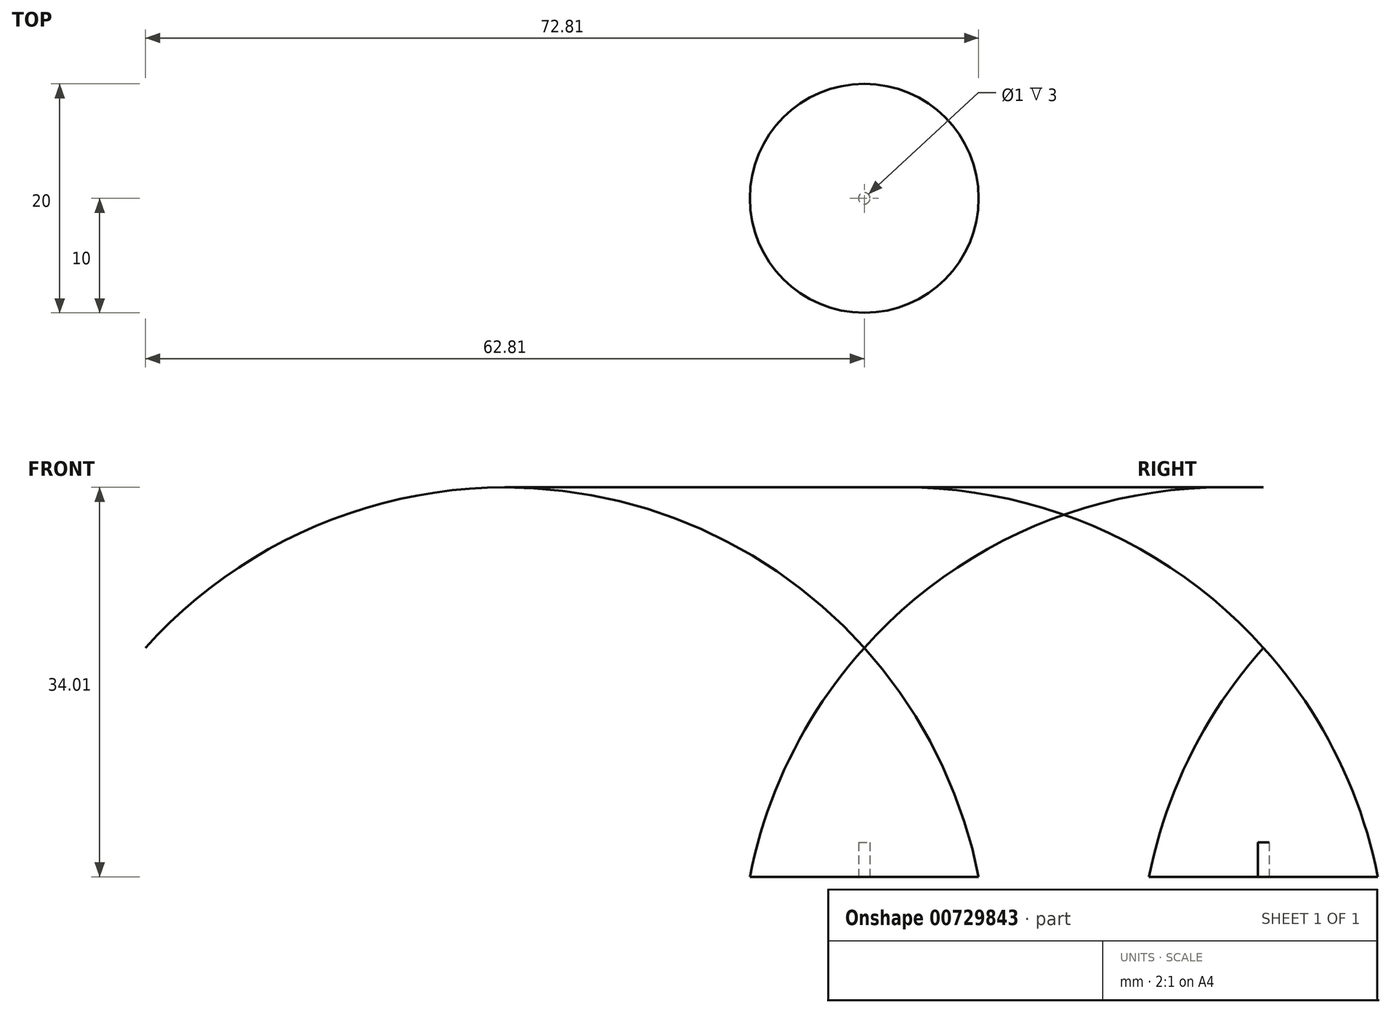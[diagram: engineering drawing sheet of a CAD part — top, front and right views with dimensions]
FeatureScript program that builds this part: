
annotation { "Feature Type Name" : "Feature", "Feature Type Description" : "" }
export const myFeature = defineFeature(function(context is Context, id is Id, definition is map)
    precondition{}
    {
        {
            var Q0;
            Q0=qCreatedBy(makeId("Front.planeOp"),FACE);
            var sketch = newSketch(context, id + "F0", { "sketchPlane" : qUnion([Q0])});
            skLineSegment(sketch, "E0", {"start": v(-0.5, 0) * mm, "end": v(-10, 0) * mm});
            skArc(sketch, "E1", {"start": v(0, 20) * mm, "mid": v(-6.35, 10.67) * mm, "end": v(-10, 0) * mm});
            skLineSegment(sketch, "E2", {"start": v(-0.5, 0) * mm, "end": v(-0.5, 3) * mm});
            skLineSegment(sketch, "E3", {"start": v(-0.5, 3) * mm, "end": v(0, 3) * mm});
            skLineSegment(sketch, "E4", {"start": v(0, 3) * mm, "end": v(0, 20) * mm});
            skSolve(sketch);
        }
        {
            var Q0;
            Q0=makeQuery(id+"F0.imprint","IMPRINT",FACE,{"disambiguationData":[TD([[makeQuery(id+"F0.imprint","IMPRINT",EDGE,{"derivedFrom":sQuery(id+"F0.wireOp",EDGE,"E0")}),-1.0]])]});
            var Q1;
            Q1=sQuery(id+"F0.wireOp",EDGE,"E4");
            revolve(context, id + "F1", {"surfaceOperationType" : NewSurfaceOperationType.NEW, "entities" : qUnion([Q0]), "axis" : qUnion([Q1]), "revolveType" : RevolveType.FULL});
        }
    });
